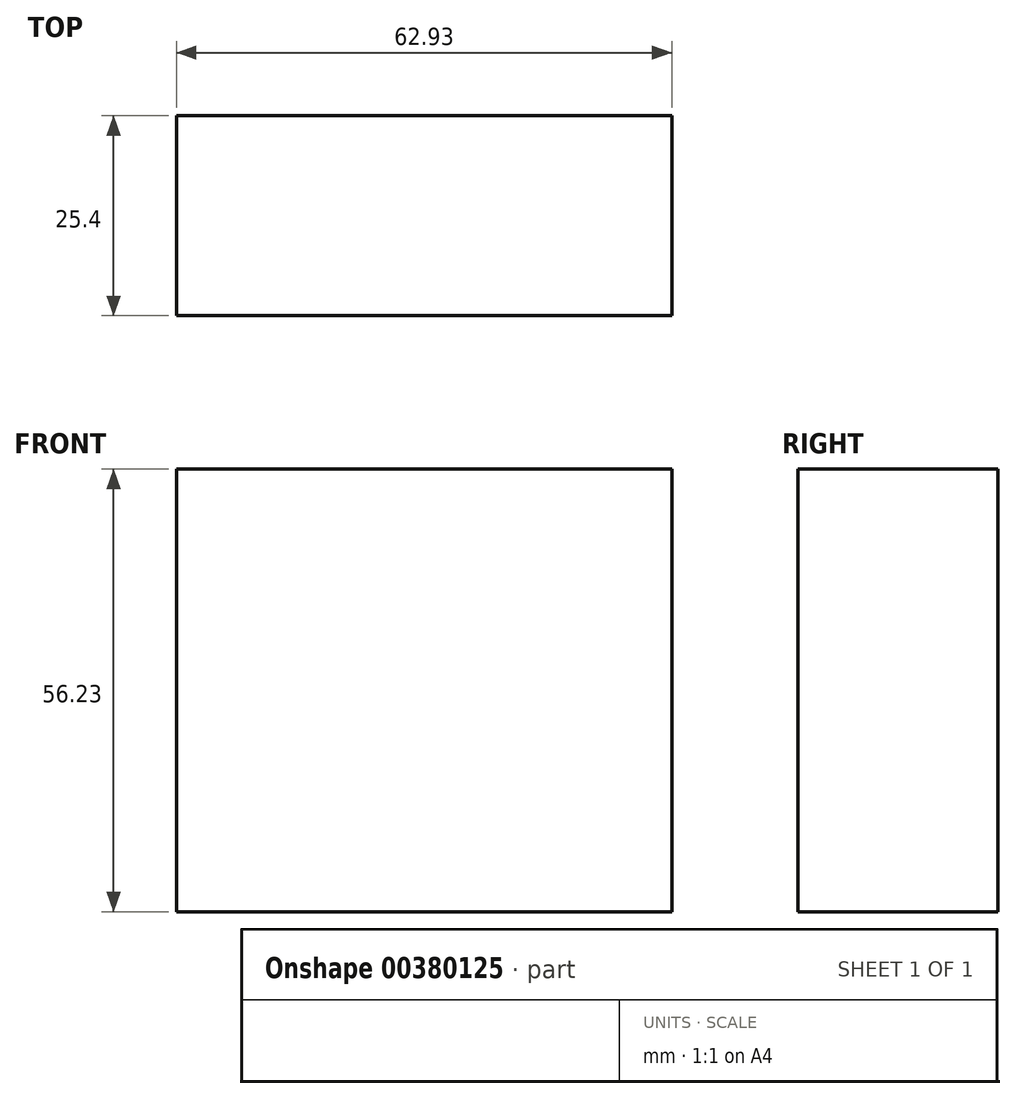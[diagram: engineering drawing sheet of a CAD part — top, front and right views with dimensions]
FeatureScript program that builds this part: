
annotation { "Feature Type Name" : "Feature", "Feature Type Description" : "" }
export const myFeature = defineFeature(function(context is Context, id is Id, definition is map)
    precondition{}
    {
        {
            var Q0;
            Q0=qCreatedBy(makeId("Front.planeOp"),FACE);
            var sketch = newSketch(context, id + "F0", { "sketchPlane" : qUnion([Q0])});
            skLineSegment(sketch, "E0.bottom", {"start": v(-20.66, 30.95) * mm, "end": v(42.27, 30.95) * mm});
            skLineSegment(sketch, "E0.top", {"start": v(-20.66, -25.28) * mm, "end": v(42.27, -25.28) * mm});
            skLineSegment(sketch, "E0.left", {"start": v(-20.66, 30.95) * mm, "end": v(-20.66, -25.28) * mm});
            skLineSegment(sketch, "E0.right", {"start": v(42.27, 30.95) * mm, "end": v(42.27, -25.28) * mm});
            skSolve(sketch);
        }
        {
            var Q0;
            Q0 = qSketchRegion(id + "F0", true);
            extrude(context, id + "F1", {"entities" : qUnion([Q0]), "depth" : 25.4 * mm});
        }
    });
